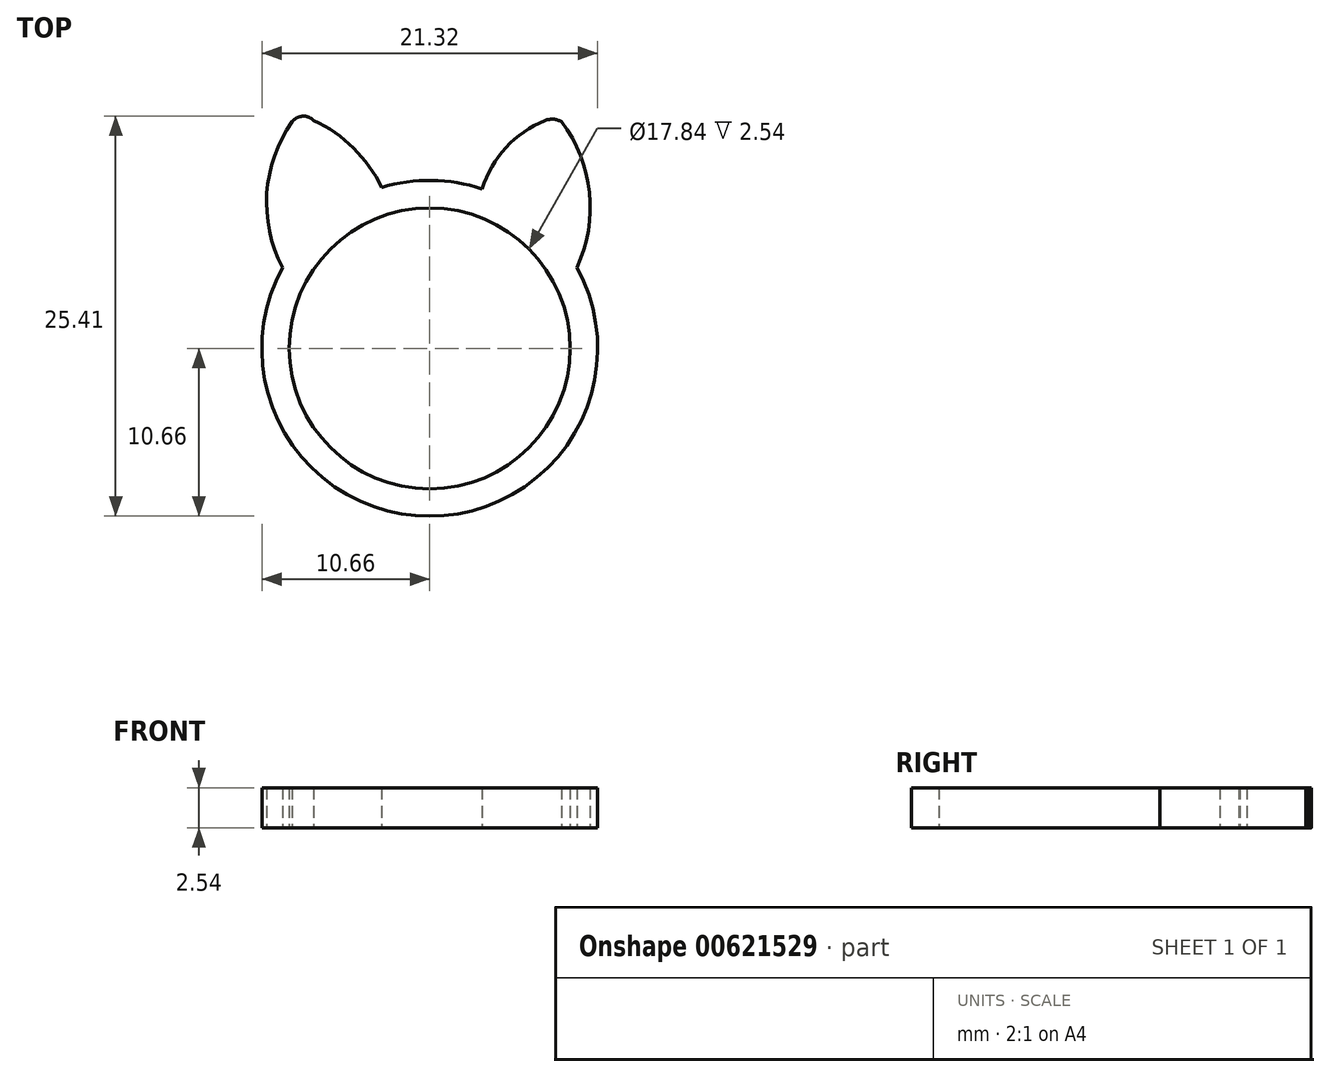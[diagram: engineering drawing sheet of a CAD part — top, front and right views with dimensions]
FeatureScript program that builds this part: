
annotation { "Feature Type Name" : "Feature", "Feature Type Description" : "" }
export const myFeature = defineFeature(function(context is Context, id is Id, definition is map)
    precondition{}
    {
        {
            var Q0;
            Q0=qCreatedBy(makeId("Top.planeOp"),FACE);
            var sketch = newSketch(context, id + "F0", { "sketchPlane" : qUnion([Q0])});
            skCircle(sketch, "E0", {"center": v(0, 0) * mm, "radius": 8.92 * mm});
            skArc(sketch, "E1", {"start": v(-9.35, 5.13) * mm, "mid": v(0, -10.66) * mm, "end": v(9.35, 5.13) * mm});
            skArc(sketch, "E2", {"start": v(9.35, 5.13) * mm, "mid": v(10.14, 9.9) * mm, "end": v(8.38, 14.4) * mm});
            skArc(sketch, "E3", {"start": v(7.33, 14.47) * mm, "mid": v(4.84, 12.75) * mm, "end": v(3.33, 10.13) * mm});
            skArc(sketch, "E4", {"start": v(8.38, 14.4) * mm, "mid": v(7.86, 14.55) * mm, "end": v(7.33, 14.47) * mm});
            skArc(sketch, "E5", {"start": v(-3.06, 10.21) * mm, "mid": v(-4.84, 12.72) * mm, "end": v(-7.36, 14.47) * mm});
            skArc(sketch, "E6", {"start": v(-8.74, 14.4) * mm, "mid": v(-10.35, 9.85) * mm, "end": v(-9.35, 5.13) * mm});
            skArc(sketch, "E7", {"start": v(-7.36, 14.47) * mm, "mid": v(-8.07, 14.75) * mm, "end": v(-8.74, 14.4) * mm});
            skArc(sketch, "E8.trimOffspring", {"start": v(3.33, 10.13) * mm, "mid": v(0.14, 10.66) * mm, "end": v(-3.06, 10.21) * mm});
            skSolve(sketch);
        }
        {
            var Q0;
            Q0 = qSketchRegion(id + "F0", true);
            extrude(context, id + "F1", {"entities" : qUnion([Q0]), "depth" : 2.54 * mm, "offsetDistance" : 25.4 * mm});
        }
    });
